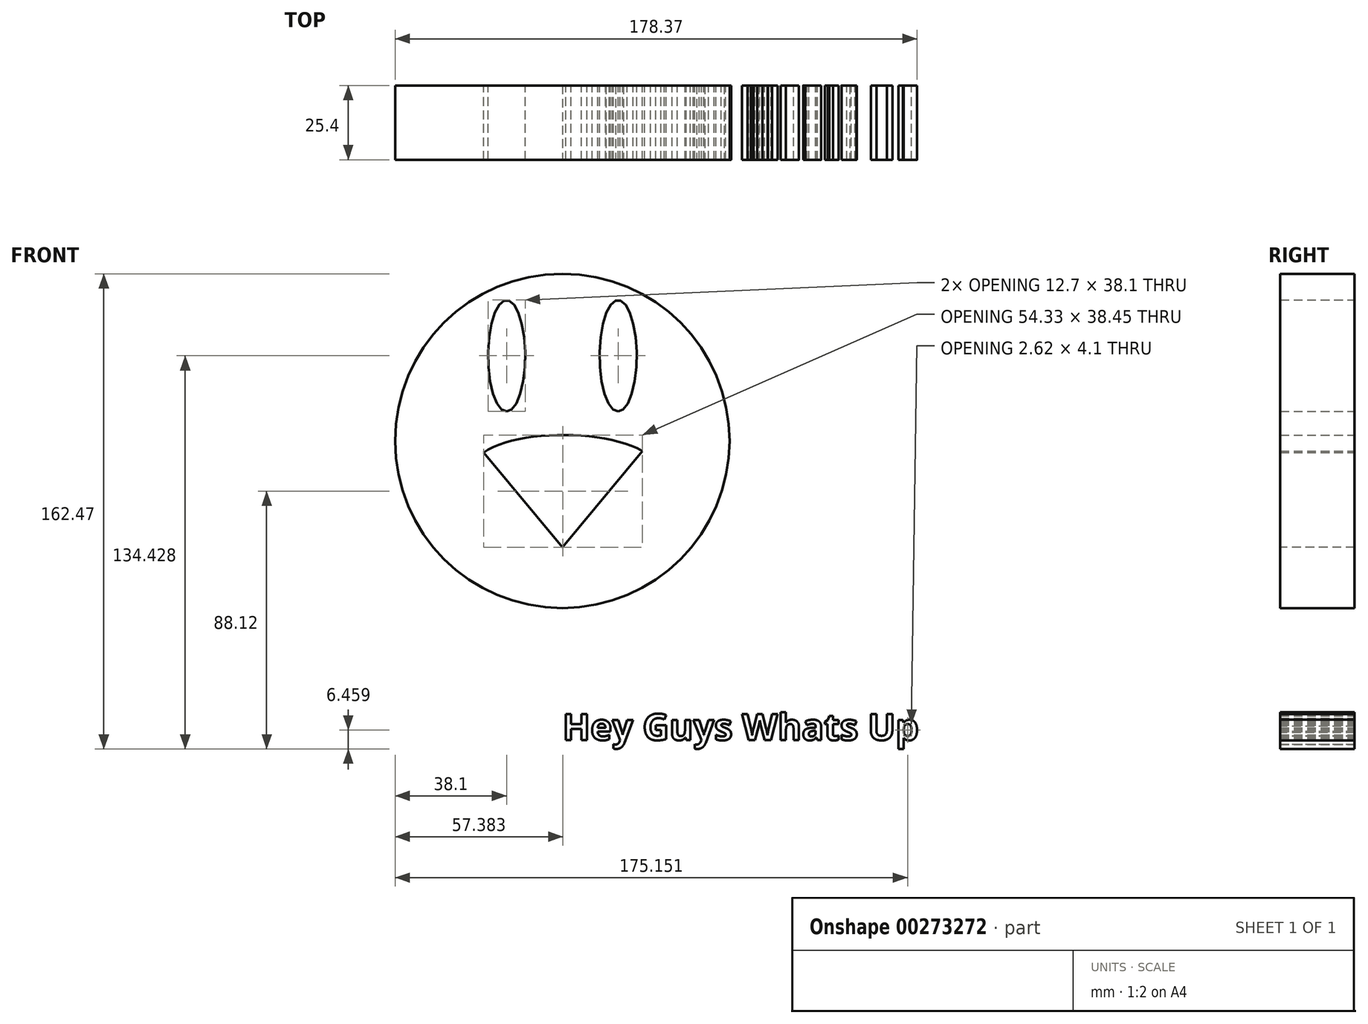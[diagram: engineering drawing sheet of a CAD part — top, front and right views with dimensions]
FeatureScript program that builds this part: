
annotation { "Feature Type Name" : "Feature", "Feature Type Description" : "" }
export const myFeature = defineFeature(function(context is Context, id is Id, definition is map)
    precondition{}
    {
        {
            var Q0;
            Q0=qCreatedBy(makeId("Front.planeOp"),FACE);
            var sketch = newSketch(context, id + "F0", { "sketchPlane" : qUnion([Q0])});
            skCircle(sketch, "E0", {"center": v(0, 0) * mm, "radius": 57.15 * mm});
            skFitSpline(sketch, "E1", {"points": [v(-29.87, -6.86) * mm, v(0, -36.42) * mm, v(32.3, -7.77) * mm, v(-29.87, -6.86) * mm]});
            skEllipse(sketch, "E2", {"center": v(-19.05, 29.1) * mm, "majorRadius": 19.05 * mm, "minorRadius": 6.35 * mm, "majorAxis": v(0, -1)});
            skEllipse(sketch, "E3", {"center": v(19.05, 29.1) * mm, "majorRadius": 19.05 * mm, "minorRadius": 6.35 * mm, "majorAxis": v(0, -1)});
            skPoint(sketch, "E4", {"position": v(19.05, 10.06) * mm});
            skPoint(sketch, "E5", {"position": v(-19.05, 10.06) * mm});
            skText(sketch, "E6", { "text": "Hey Guys Whats Up\n", "fontName": "OpenSans-Bold.ttf"});
            const initialGuessF0  = {"E6": [0, -0.1023, 1, 0, 0.00904]};
            skSetInitialGuess(sketch, initialGuessF0);
            skSolve(sketch);
        }
        {
            var Q0;
            Q0=makeQuery(id+"F0.imprint","IMPRINT",FACE,{"disambiguationData":[TD([[makeQuery(id+"F0.imprint","IMPRINT",EDGE,{"derivedFrom":sQuery(id+"F0.wireOp",EDGE,"E0")}),1.0]])]});
            extrude(context, id + "F1", {"entities" : qUnion([Q0]), "depth" : 25.4 * mm});
        }
        {
            var Q0;
            Q0 = qSketchRegion(id + "F0", true);
            extrude(context, id + "F2", {"entities" : qUnion([Q0]), "operationType" : NewBodyOperationType.ADD, "depth" : 25.4 * mm});
        }
        {
            var Q0;
            Q0=makeQuery(id+"F1.opExtrude","CAP_FACE",FACE,{"disambiguationData":[OSD([sQuery(id+"F0.wireOp",EDGE,"E0"),sQuery(id+"F0.wireOp",EDGE,"E1"),sQuery(id+"F0.wireOp",EDGE,"E2"),sQuery(id+"F0.wireOp",EDGE,"E3")])],"isStart":false});
            var sketch = newSketch(context, id + "F3", { "sketchPlane" : qUnion([Q0])});
            skLineSegment(sketch, "E7", {"start": v(-95.25, 78.27) * mm, "end": v(0, -36.42) * mm});
            skLineSegment(sketch, "E8", {"start": v(0, -36.42) * mm, "end": v(95.25, 78.27) * mm});
            skLineSegment(sketch, "E9", {"start": v(95.25, 78.27) * mm, "end": v(95.25, 0) * mm});
            skLineSegment(sketch, "E10", {"start": v(95.25, 0) * mm, "end": v(0, -79.1) * mm});
            skLineSegment(sketch, "E11", {"start": v(0, -79.1) * mm, "end": v(-95.25, 0) * mm});
            skLineSegment(sketch, "E12", {"start": v(-95.25, 0) * mm, "end": v(-95.25, 78.27) * mm});
            skSolve(sketch);
        }
        {
            var Q0;
            {var subQ0=sQuery(id+"F3.wireOp",EDGE,"E7");var subQ1=makeQuery(id+"F1.opExtrude","CAP_EDGE",EDGE,{"disambiguationData":[OSD([sQuery(id+"F0.wireOp",EDGE,"E1")])],"isStart":false});var subQ3=makeQuery(id+"F3.imprint","INTERSECT",VERTEX,{"derivedFrom":[subQ1,subQ0]});Q0=makeQuery(id+"F3.imprint","IMPRINT",FACE,{"disambiguationData":[TD([[makeQuery(id+"F3.imprint","IMPRINT",EDGE,{"disambiguationData":[TD([[subQ3,-1.0]])],"derivedFrom":subQ0}),-1.0]])]});}
            var Q1;
            {var subQ0=sQuery(id+"F3.wireOp",EDGE,"E8");var subQ1=makeQuery(id+"F1.opExtrude","CAP_EDGE",EDGE,{"disambiguationData":[OSD([sQuery(id+"F0.wireOp",EDGE,"E1")])],"isStart":false});var subQ3=makeQuery(id+"F3.imprint","INTERSECT",VERTEX,{"derivedFrom":[subQ1,subQ0]});Q1=makeQuery(id+"F3.imprint","IMPRINT",FACE,{"disambiguationData":[TD([[makeQuery(id+"F3.imprint","IMPRINT",EDGE,{"disambiguationData":[TD([[subQ3,1.0]])],"derivedFrom":subQ0}),-1.0]])]});}
            var Q2;
            {var subQ1=sQuery(id+"F3.wireOp",EDGE,"E7");var subQ5=makeQuery(id+"F1.opExtrude","CAP_EDGE",EDGE,{"disambiguationData":[OSD([sQuery(id+"F0.wireOp",EDGE,"E0")])],"isStart":false});var subQ8=makeQuery(id+"F3.imprint","INTERSECT",VERTEX,{"derivedFrom":[subQ5,subQ1]});Q2=makeQuery(id+"F3.imprint","IMPRINT",FACE,{"disambiguationData":[TD([[makeQuery(id+"F3.imprint","IMPRINT",EDGE,{"disambiguationData":[TD([[subQ8,-1.0]])],"derivedFrom":subQ1}),-1.0]])]});}
            extrude(context, id + "F4", {"entities" : qUnion([Q0, Q1, Q2]), "operationType" : NewBodyOperationType.ADD, "oppositeDirection" : true, "depth" : 25.4 * mm});
        }
    });
